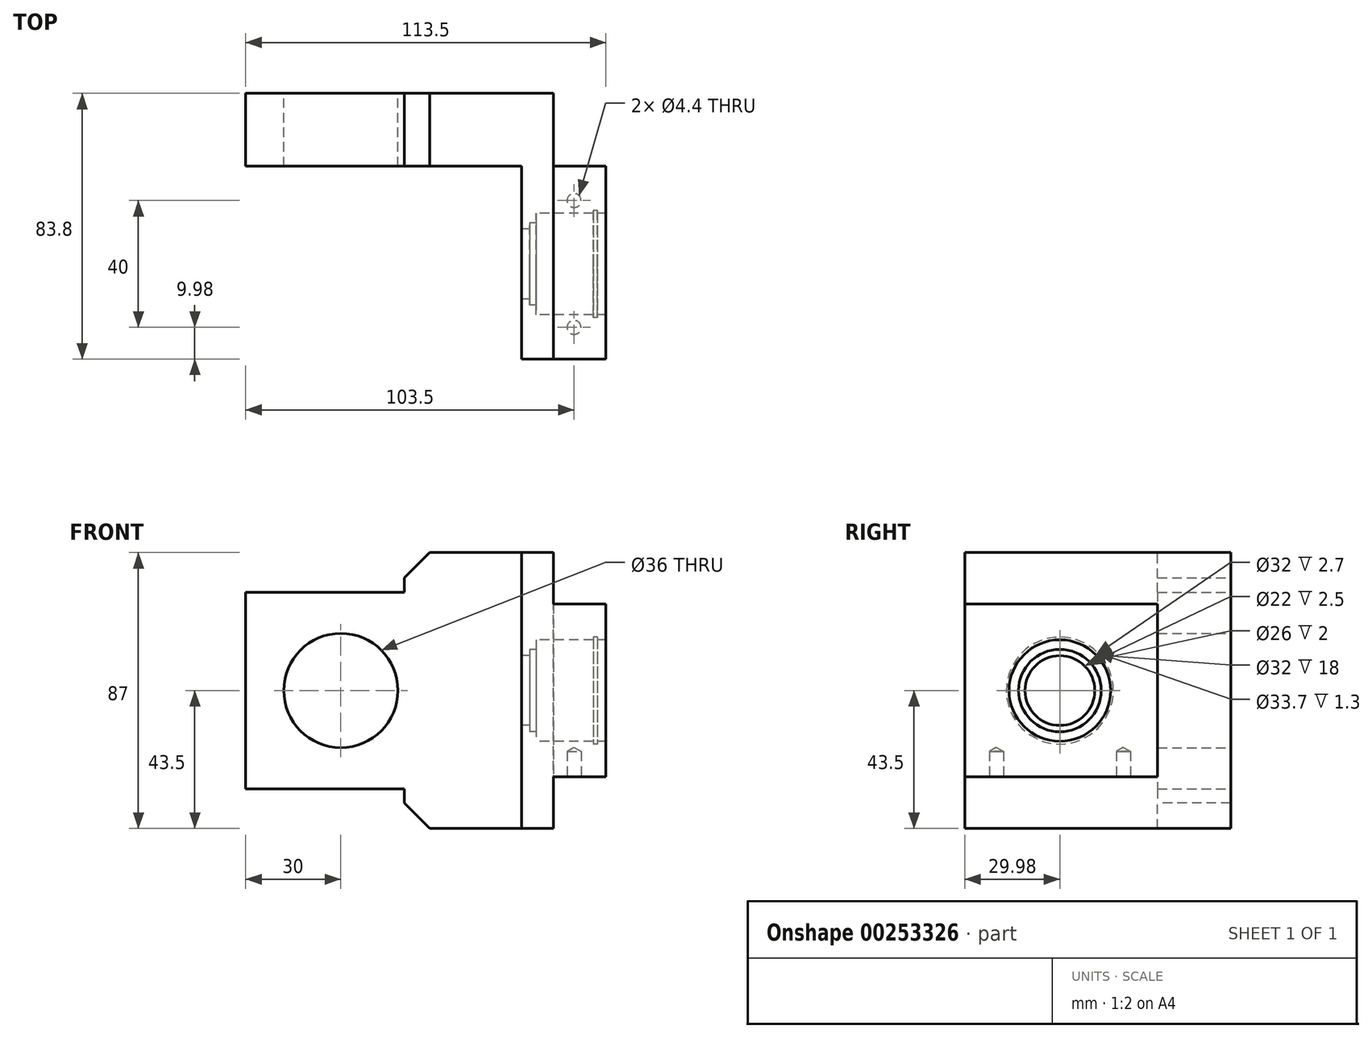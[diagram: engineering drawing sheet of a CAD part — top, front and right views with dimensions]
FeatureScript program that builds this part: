
annotation { "Feature Type Name" : "Feature", "Feature Type Description" : "" }
export const myFeature = defineFeature(function(context is Context, id is Id, definition is map)
    precondition{}
    {
        {
            var Q0;
            Q0=qCreatedBy(makeId("Front.planeOp"),FACE);
            var sketch = newSketch(context, id + "F0", { "sketchPlane" : qUnion([Q0])});
            skLineSegment(sketch, "E0", {"start": v(-30, -31) * mm, "end": v(20, -31) * mm});
            skLineSegment(sketch, "E1", {"start": v(20, -31) * mm, "end": v(20, -43.5) * mm});
            skLineSegment(sketch, "E2", {"start": v(20, -43.5) * mm, "end": v(67, -43.5) * mm});
            skLineSegment(sketch, "E3", {"start": v(67, -43.5) * mm, "end": v(67, -27.25) * mm});
            skLineSegment(sketch, "E4", {"start": v(67, -27.25) * mm, "end": v(83.5, -27.25) * mm});
            skLineSegment(sketch, "E5.MirrorCS", {"start": v(67, 27.25) * mm, "end": v(83.5, 27.25) * mm});
            skLineSegment(sketch, "E6.MirrorCS", {"start": v(-30, 31) * mm, "end": v(20, 31) * mm});
            skLineSegment(sketch, "E7.MirrorCS", {"start": v(67, 43.5) * mm, "end": v(67, 27.25) * mm});
            skLineSegment(sketch, "E8.MirrorCS", {"start": v(20, 43.5) * mm, "end": v(67, 43.5) * mm});
            skLineSegment(sketch, "E9.MirrorCS", {"start": v(20, 31) * mm, "end": v(20, 43.5) * mm});
            skLineSegment(sketch, "E10", {"start": v(-30, 31) * mm, "end": v(-30, -31) * mm});
            skLineSegment(sketch, "E11", {"start": v(83.5, 27.25) * mm, "end": v(83.5, -27.25) * mm});
            skCircle(sketch, "E12", {"center": v(0, 0) * mm, "radius": 18 * mm});
            skLineSegment(sketch, "E13", {"start": v(57, 43.5) * mm, "end": v(57, -43.5) * mm});
            skLineSegment(sketch, "E14", {"start": v(67, 27.25) * mm, "end": v(67, -27.25) * mm});
            skSolve(sketch);
        }
        {
            var Q0;
            Q0=makeQuery(id+"F0.imprint","IMPRINT",FACE,{"disambiguationData":[TD([[makeQuery(id+"F0.imprint","IMPRINT",EDGE,{"derivedFrom":sQuery(id+"F0.wireOp",EDGE,"E0")}),1.0]])]});
            extrude(context, id + "F1", {"entities" : qUnion([Q0]), "depth" : 23 * mm});
        }
        {
            var Q0;
            {var subQ3=sQuery(id+"F0.wireOp",EDGE,"E3");Q0=makeQuery(id+"F0.imprint","IMPRINT",FACE,{"disambiguationData":[TD([[makeQuery(id+"F0.imprint","IMPRINT",EDGE,{"derivedFrom":subQ3}),1.0]])]});}
            extrude(context, id + "F2", {"entities" : qUnion([Q0]), "operationType" : NewBodyOperationType.ADD, "depth" : (23 + 60.8) * mm});
        }
        {
            var Q0;
            Q0=makeQuery(id+"F0.imprint","IMPRINT",FACE,{"disambiguationData":[TD([[makeQuery(id+"F0.imprint","IMPRINT",EDGE,{"derivedFrom":sQuery(id+"F0.wireOp",EDGE,"E4")}),1.0]])]});
            extrude(context, id + "F3", {"entities" : qUnion([Q0]), "operationType" : NewBodyOperationType.ADD, "depth" : (60.8 + 23) * mm, "hasSecondDirection" : true, "secondDirectionOppositeDirection" : false, "secondDirectionDepth" : 23 * mm});
        }
        {
            var Q0;
            Q0=qCreatedBy(makeId("Top.planeOp"),FACE);
            var sketch = newSketch(context, id + "F4", { "sketchPlane" : qUnion([Q0])});
            skLineSegment(sketch, "E15.0", {"start": v(57, -64.82) * mm, "end": v(57, -53.82) * mm});
            skLineSegment(sketch, "E16.0", {"start": v(83.5, -69.82) * mm, "end": v(83.5, -53.82) * mm});
            skLineSegment(sketch, "E17", {"start": v(83.5, -69.82) * mm, "end": v(80.8, -69.82) * mm});
            skLineSegment(sketch, "E18", {"start": v(80.8, -69.82) * mm, "end": v(80.8, -70.67) * mm});
            skLineSegment(sketch, "E19", {"start": v(80.8, -70.67) * mm, "end": v(79.5, -70.67) * mm});
            skLineSegment(sketch, "E20", {"start": v(79.5, -70.67) * mm, "end": v(79.5, -69.82) * mm});
            skLineSegment(sketch, "E21", {"start": v(79.5, -69.82) * mm, "end": v(61.5, -69.82) * mm});
            skLineSegment(sketch, "E22", {"start": v(61.5, -69.82) * mm, "end": v(61.5, -66.82) * mm});
            skLineSegment(sketch, "E23", {"start": v(61.5, -66.82) * mm, "end": v(59.5, -66.82) * mm});
            skLineSegment(sketch, "E24", {"start": v(59.5, -66.82) * mm, "end": v(59.5, -64.82) * mm});
            skLineSegment(sketch, "E25", {"start": v(59.5, -64.82) * mm, "end": v(57, -64.82) * mm});
            skLineSegment(sketch, "E26", {"start": v(96.15, -53.82) * mm, "end": v(-7.85, -53.82) * mm, "construction": true});
            skLineSegment(sketch, "E27.MirrorCS", {"start": v(61.5, -37.82) * mm, "end": v(61.5, -40.82) * mm, "construction": true});
            skLineSegment(sketch, "E28.MirrorCS", {"start": v(79.5, -36.97) * mm, "end": v(79.5, -37.82) * mm, "construction": true});
            skLineSegment(sketch, "E29.MirrorCS", {"start": v(80.8, -36.97) * mm, "end": v(79.5, -36.97) * mm, "construction": true});
            skLineSegment(sketch, "E30.MirrorCS", {"start": v(61.5, -40.82) * mm, "end": v(59.5, -40.82) * mm, "construction": true});
            skLineSegment(sketch, "E31.MirrorCS", {"start": v(59.5, -40.82) * mm, "end": v(59.5, -42.82) * mm, "construction": true});
            skLineSegment(sketch, "E32.MirrorCS", {"start": v(80.8, -37.82) * mm, "end": v(80.8, -36.97) * mm, "construction": true});
            skLineSegment(sketch, "E33.MirrorCS", {"start": v(83.5, -37.82) * mm, "end": v(80.8, -37.82) * mm, "construction": true});
            skLineSegment(sketch, "E34.MirrorCS", {"start": v(79.5, -37.82) * mm, "end": v(61.5, -37.82) * mm, "construction": true});
            skLineSegment(sketch, "E35.MirrorCS", {"start": v(59.5, -42.82) * mm, "end": v(57, -42.82) * mm, "construction": true});
            skLineSegment(sketch, "E36.MirrorCS", {"start": v(83.5, -53.82) * mm, "end": v(83.5, -69.82) * mm});
            skPoint(sketch, "E37.orphan", {"position": v(83.5, -23.84) * mm});
            skLineSegment(sketch, "E38.trimOffspring", {"start": v(83.5, -23.84) * mm, "end": v(83.5, -23) * mm});
            skLineSegment(sketch, "E39.trimOffspring", {"start": v(57, -23.84) * mm, "end": v(57, -23) * mm});
            skPoint(sketch, "E40.orphan", {"position": v(57, -83.8) * mm});
            skLineSegment(sketch, "E41.trimOffspring", {"start": v(83.5, -83.8) * mm, "end": v(83.5, -84.64) * mm});
            skLineSegment(sketch, "E42.trimOffspring", {"start": v(57, -83.8) * mm, "end": v(57, -84.64) * mm});
            skLineSegment(sketch, "E43", {"start": v(57, -53.82) * mm, "end": v(57, -64.82) * mm});
            skLineSegment(sketch, "E44", {"start": v(57, -53.82) * mm, "end": v(57, -42.82) * mm, "construction": true});
            skLineSegment(sketch, "E45", {"start": v(83.5, -53.82) * mm, "end": v(83.5, -37.82) * mm, "construction": true});
            skLineSegment(sketch, "E46", {"start": v(83.5, -53.82) * mm, "end": v(57, -53.82) * mm});
            skSolve(sketch);
        }
        {
            var Q0;
            Q0 = qSketchRegion(id + "F4", true);
            var Q1;
            Q1=sQuery(id+"F4.wireOp",EDGE,"E46");
            revolve(context, id + "F5", {"operationType" : NewBodyOperationType.REMOVE, "entities" : qUnion([Q0]), "axis" : qUnion([Q1]), "revolveType" : RevolveType.FULL, "oppositeDirection" : true});
        }
        {
            var Q0;
            Q0=makeQuery(id+"F1.opExtrude","SWEPT_EDGE",EDGE,{"disambiguationData":[OSD([sQuery(id+"F0.wireOp",EDGE,"E8.MirrorCS"),sQuery(id+"F0.wireOp",EDGE,"E9.MirrorCS")])]});
            var Q1;
            Q1=makeQuery(id+"F1.opExtrude","SWEPT_EDGE",EDGE,{"disambiguationData":[OSD([sQuery(id+"F0.wireOp",EDGE,"E1"),sQuery(id+"F0.wireOp",EDGE,"E2")])]});
            chamfer(context, id + "F6", {"entities" : qUnion([Q0, Q1]), "chamferType" : ChamferType.OFFSET_ANGLE, "width" : 8 * mm, "oppositeDirection" : false, "angle" : 45 * degree, "tangentPropagation" : true});
        }
        {
            var Q0;
            Q0=makeQuery(id+"F3.opExtrude","SWEPT_FACE",FACE,{"disambiguationData":[OSD([sQuery(id+"F0.wireOp",EDGE,"E4")])]});
            var sketch = newSketch(context, id + "F7", { "sketchPlane" : qUnion([Q0])});
            skPoint(sketch, "E47", {"position": v(73.5, 73.82) * mm});
            skPoint(sketch, "E48", {"position": v(73.5, 33.82) * mm});
            skSolve(sketch);
        }
        {
            var Q0;
            Q0=sQuery(id+"F7.wireOp",VERTEX,"E47");
            var Q1;
            Q1=sQuery(id+"F7.wireOp",VERTEX,"E48");
            var Q2;
            Q2=makeQuery(id+"F1.opExtrude","SWEPT_BODY",BODY,{"disambiguationData":[OSD([sQuery(id+"F0.wireOp",EDGE,"E0"),sQuery(id+"F0.wireOp",EDGE,"E1"),sQuery(id+"F0.wireOp",EDGE,"E2"),sQuery(id+"F0.wireOp",EDGE,"E6.MirrorCS"),sQuery(id+"F0.wireOp",EDGE,"E8.MirrorCS"),sQuery(id+"F0.wireOp",EDGE,"E9.MirrorCS"),sQuery(id+"F0.wireOp",EDGE,"E10"),sQuery(id+"F0.wireOp",EDGE,"E12"),sQuery(id+"F0.wireOp",EDGE,"E13")])]});
            hole(context, id + "F8", {"style" : HoleStyle.SIMPLE, "endStyle" : HoleEndStyle.BLIND, "standardTappedOrClearance" : lookupTablePath({ "standard" : "ISO", "fit" : "Normal", "size" : "M4", "type" : "Clearance" }), "standardBlindInLast" : lookupTablePath({ "fit" : "Standard", "standard" : "ISO", "size" : "M4", "type" : "Clearance" }), "holeDiameter" : 4.4 * mm, "holeDepth" : 8 * mm, "tappedDepth" : 12 * mm, "tapClearance" : 3, "locations" : qUnion([Q0, Q1]), "scope" : qUnion([Q2])});
        }
    });
